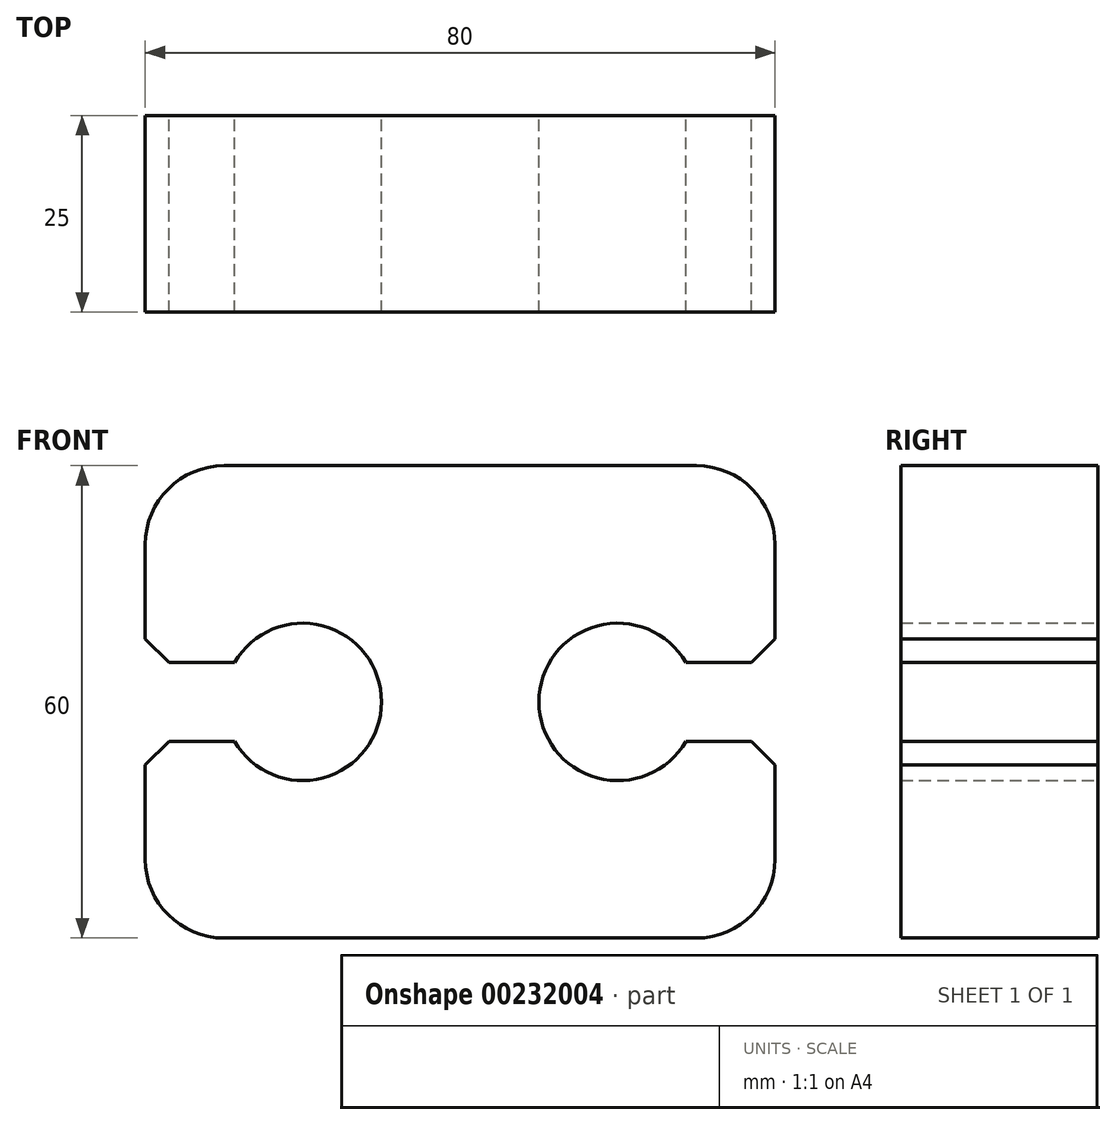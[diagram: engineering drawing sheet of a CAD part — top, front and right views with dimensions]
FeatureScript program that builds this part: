
annotation { "Feature Type Name" : "Feature", "Feature Type Description" : "" }
export const myFeature = defineFeature(function(context is Context, id is Id, definition is map)
    precondition{}
    {
        {
            var Q0;
            Q0=qCreatedBy(makeId("Front.planeOp"),FACE);
            var sketch = newSketch(context, id + "F0", { "sketchPlane" : qUnion([Q0])});
            skArc(sketch, "E0", {"start": v(-28.66, -5) * mm, "mid": v(-10, 0) * mm, "end": v(-28.66, 5) * mm});
            skLineSegment(sketch, "E1", {"start": v(-28.66, 5) * mm, "end": v(-37, 5) * mm});
            skLineSegment(sketch, "E2", {"start": v(-37, 5) * mm, "end": v(-40, 8) * mm});
            skLineSegment(sketch, "E3", {"start": v(-40, 8) * mm, "end": v(-40, 20) * mm});
            skLineSegment(sketch, "E4", {"start": v(-30, 30) * mm, "end": v(0, 30) * mm});
            skPoint(sketch, "E5.visualSharp", {"position": v(-40, 30) * mm});
            skArc(sketch, "E5.filletArc", {"start": v(-30, 30) * mm, "mid": v(-37.07, 27.07) * mm, "end": v(-40, 20) * mm});
            skLineSegment(sketch, "E6.MirrorCS", {"start": v(-28.66, -5) * mm, "end": v(-37, -5) * mm});
            skLineSegment(sketch, "E7.MirrorCS", {"start": v(-37, -5) * mm, "end": v(-40, -8) * mm});
            skLineSegment(sketch, "E8.MirrorCS", {"start": v(-40, -8) * mm, "end": v(-40, -20) * mm});
            skArc(sketch, "E9.MirrorCS", {"start": v(-30, -30) * mm, "mid": v(-37.07, -27.07) * mm, "end": v(-40, -20) * mm});
            skLineSegment(sketch, "E10.MirrorCS", {"start": v(-30, -30) * mm, "end": v(0, -30) * mm});
            skLineSegment(sketch, "E11.MirrorCS", {"start": v(37, 5) * mm, "end": v(40, 8) * mm});
            skLineSegment(sketch, "E12.MirrorCS", {"start": v(37, -5) * mm, "end": v(40, -8) * mm});
            skLineSegment(sketch, "E13.MirrorCS", {"start": v(28.66, 5) * mm, "end": v(37, 5) * mm});
            skPoint(sketch, "E14.MirrorP", {"position": v(40, 30) * mm});
            skLineSegment(sketch, "E15.MirrorCS", {"start": v(28.66, -5) * mm, "end": v(37, -5) * mm});
            skArc(sketch, "E16.MirrorCS", {"start": v(28.66, -5) * mm, "mid": v(10, 0) * mm, "end": v(28.66, 5) * mm});
            skArc(sketch, "E17.MirrorCS", {"start": v(30, -30) * mm, "mid": v(37.07, -27.07) * mm, "end": v(40, -20) * mm});
            skArc(sketch, "E18.MirrorCS", {"start": v(30, 30) * mm, "mid": v(37.07, 27.07) * mm, "end": v(40, 20) * mm});
            skLineSegment(sketch, "E19.MirrorCS", {"start": v(40, -8) * mm, "end": v(40, -20) * mm});
            skLineSegment(sketch, "E20.MirrorCS", {"start": v(30, -30) * mm, "end": v(0, -30) * mm});
            skLineSegment(sketch, "E21.MirrorCS", {"start": v(40, 8) * mm, "end": v(40, 20) * mm});
            skLineSegment(sketch, "E22.MirrorCS", {"start": v(30, 30) * mm, "end": v(0, 30) * mm});
            skSolve(sketch);
        }
        {
            var Q0;
            Q0=makeQuery(id+"F0.imprint","IMPRINT",FACE,{"disambiguationData":[TD([[makeQuery(id+"F0.imprint","IMPRINT",EDGE,{"derivedFrom":sQuery(id+"F0.wireOp",EDGE,"E0")}),-1.0]])]});
            extrude(context, id + "F1", {"entities" : qUnion([Q0]), "depth" : 25 * mm});
        }
    });
